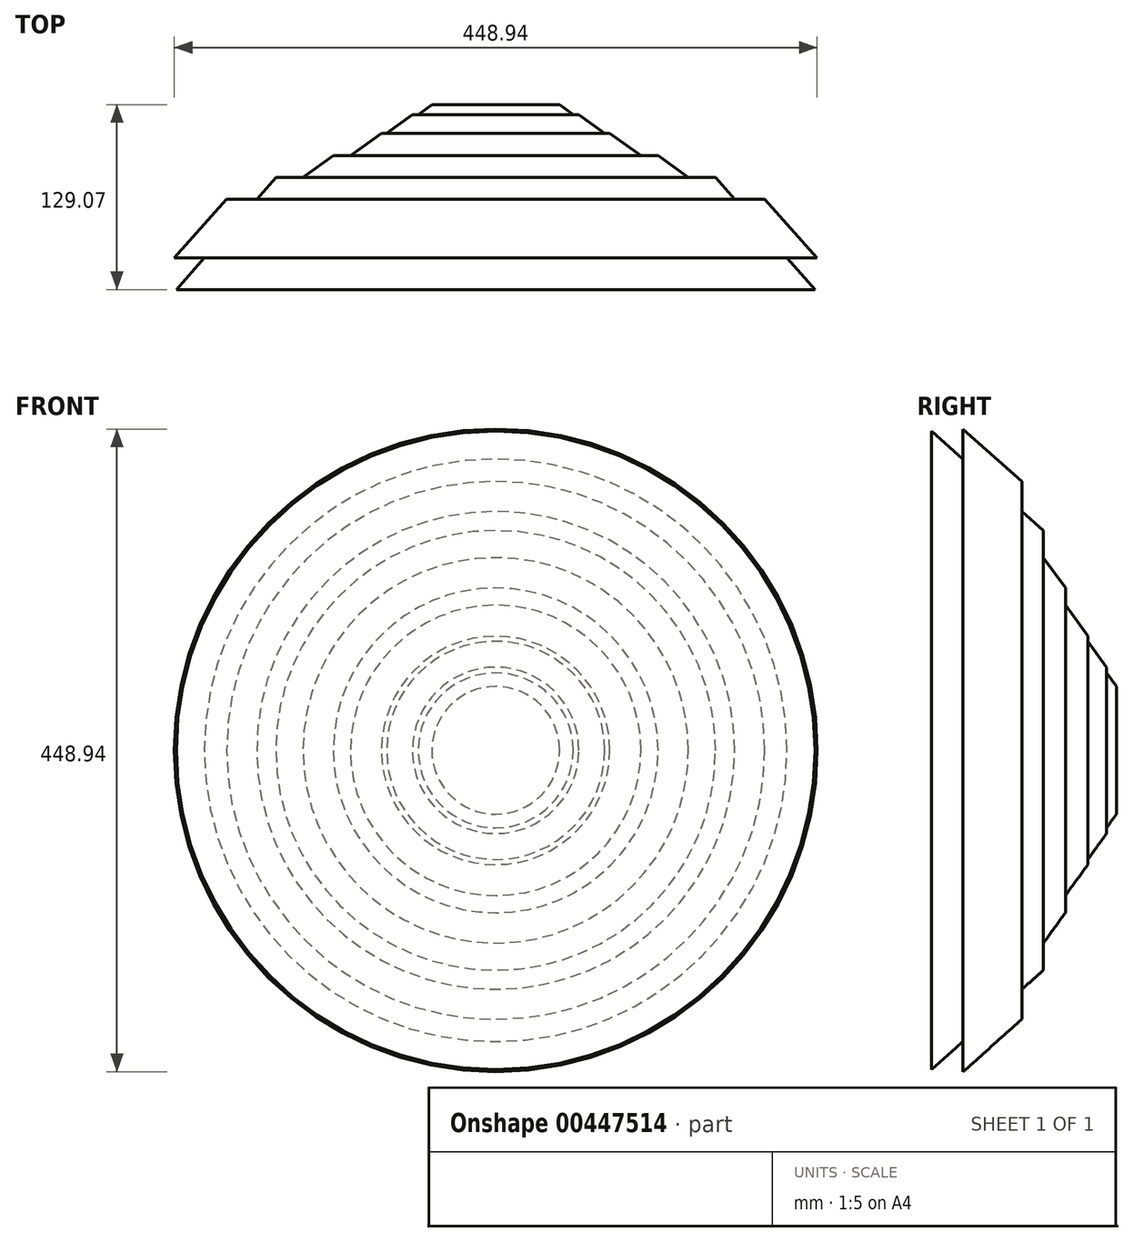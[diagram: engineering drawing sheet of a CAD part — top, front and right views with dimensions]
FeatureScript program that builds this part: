
annotation { "Feature Type Name" : "Feature", "Feature Type Description" : "" }
export const myFeature = defineFeature(function(context is Context, id is Id, definition is map)
    precondition{}
    {
        {
            var Q0;
            Q0=qCreatedBy(makeId("Top.planeOp"),FACE);
            var sketch = newSketch(context, id + "F0", { "sketchPlane" : qUnion([Q0])});
            skLineSegment(sketch, "E0", {"start": v(0, 0) * mm, "end": v(0, 25.52) * mm});
            skLineSegment(sketch, "E1", {"start": v(-25.4, 50.92) * mm, "end": v(-44.6, 50.92) * mm});
            skLineSegment(sketch, "E2", {"start": v(-44.6, 50.92) * mm, "end": v(-223.01, -78.15) * mm});
            skLineSegment(sketch, "E3", {"start": v(-223.01, -78.15) * mm, "end": v(0, -78.15) * mm});
            skLineSegment(sketch, "E4", {"start": v(0, -78.15) * mm, "end": v(0, 0) * mm});
            skLineSegment(sketch, "E5", {"start": v(-223.01, -78.15) * mm, "end": v(-153.54, 0) * mm});
            skLineSegment(sketch, "E6", {"start": v(-153.54, 0) * mm, "end": v(0, 0) * mm});
            skLineSegment(sketch, "E7", {"start": v(-134.6, 0) * mm, "end": v(-113.44, 15.3) * mm});
            skLineSegment(sketch, "E8", {"start": v(-113.44, 15.3) * mm, "end": v(0, 15.3) * mm});
            skLineSegment(sketch, "E9", {"start": v(0, 15.3) * mm, "end": v(-101.44, 15.3) * mm});
            skLineSegment(sketch, "E10", {"start": v(-101.44, 15.3) * mm, "end": v(-79.77, 30.99) * mm});
            skLineSegment(sketch, "E11", {"start": v(-79.77, 30.99) * mm, "end": v(0, 30.99) * mm});
            skLineSegment(sketch, "E12", {"start": v(0, 30.99) * mm, "end": v(-79.77, 30.99) * mm});
            skLineSegment(sketch, "E13", {"start": v(-76.18, 30.99) * mm, "end": v(-58.13, 44.05) * mm});
            skLineSegment(sketch, "E14", {"start": v(-58.13, 44.05) * mm, "end": v(0, 44.05) * mm});
            skLineSegment(sketch, "E15", {"start": v(0, -15) * mm, "end": v(-187.88, -15) * mm});
            skLineSegment(sketch, "E16", {"start": v(-187.88, -15) * mm, "end": v(-224.47, -56.16) * mm});
            skLineSegment(sketch, "E17", {"start": v(-224.47, -56.16) * mm, "end": v(0, -56.16) * mm});
            skPoint(sketch, "E18.visualSharp", {"position": v(0, 50.92) * mm});
            skArc(sketch, "E18.filletArc", {"start": v(0, 25.52) * mm, "mid": v(-7.44, 43.48) * mm, "end": v(-25.4, 50.92) * mm});
            skPoint(sketch, "E19.1.internal.snap0", {"position": v(-133.8, -13.62) * mm});
            skPoint(sketch, "E20.startSnap0", {"position": v(0, -39.08) * mm});
            skSolve(sketch);
        }
        {
            var Q0;
            Q0 = qSketchRegion(id + "F0", true);
            var Q1;
            Q1=sQuery(id+"F0.wireOp",EDGE,"E0");
            revolve(context, id + "F1", {"entities" : qUnion([Q0]), "axis" : qUnion([Q1]), "revolveType" : RevolveType.FULL});
        }
    });
